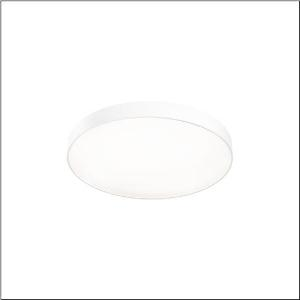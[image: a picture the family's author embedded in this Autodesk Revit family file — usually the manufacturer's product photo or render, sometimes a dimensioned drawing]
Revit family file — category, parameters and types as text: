
# Revit family: round_21_m_51mr36gm8321w
name_source: partatom
category: Lighting Fixtures
units: mm (PartAtom-declared; Revit-internal decimal feet)

## family parameters
Cut with Voids When Loaded = No
Host = Face
Light Source = No
Part Type = Normal
Room Calculation Point = No
Round Connector Dimension = Use Diameter
Shared = No

## types (1)
- --- (1 x LED, 8610 lm, 62.3 W, 3000K)
    Apparent Load = 62 VA
    CIE Flux Codes = 49 80 96 85 100
    Color Rendering = 80
    Color Temperature = 3000K
    Default Elevation = 1800 mm
    Description = Round 21 M, wall and ceiling luminaire, primary optical cover: cover, of PMMA, opal, light emission: direct/indirect distribution, primary light characteristic: symmetric, installation type: suspended mounting, surface-mounted, LED, rated luminous flux: 7.820lm, luminous efficacy: 129lm/W, light colour: 830, colour temperature: 3000K, with terminal, 3-pole, mains connection: 230V, AC, 50/60Hz, rated input power: 61W, housing, of aluminium, coated, white, diameter: 600mm, height: 62mm, protection rating (complete): IP40, insulation class (complete): insulation class I (protective earthing), certification: CE, impact resistance: IK04, permissible operating ambient temperature: -10..+35°C, packaging unit: 1 piece
    Height = 87 mm
    Lamp = 1 x LED
    Lamp Light Flux = 8610 lm
    Lamp Power = 62.3 W
    Lamp count = 1
    Length = 600 mm
    Luminous efficacy = 138 lm/W
    Manufacturer = Siteco
    ModVariant = No
    Model = 51MR36GM8321W
    Mounting Place = Ceiling
    Mounting Type = Surface mounted
    Number of Poles = 1
    OnlyDefault = Yes
    Power Factor = 1
    Product Name = Round 21 M
    Product group = wall and ceiling luminaire
    ProductGroupID = 303
    Protection Class = Protection class I
    Protection Degree = IP 40
    RLX_Detail_Level = 1
    RLX_Emergency_Light_Flux = 0 lm
    RLX_Emergency_Type = 0
    RLX_Emergency_Type_DB = No
    RlxData = <blob elided: 14749 chars, md5=6ae64f1e>
    Socket = socket
    Standby Power = 0 W
    System Light Flux = 8610 lm
    System Power = 62 W
    Type Comments = factory setting: luminous flux: 100 % | (ON | ON | ON | ON) | 700 mA
    Type Image = l_1258330.jpg
    URL = http://relux.com
    VarID = @adj_001133
    Voltage = 0 V
    Weight = 0.00 kg
    Width = 0 mm  [stored 0 ft]

note: [stored X ft] marks values corroborated as IEEE doubles in the binary element streams (Revit-internal decimal feet)

## geometry (parser evidence)
native form markers: Sweep x13
no freeform markers — native parametric forms only
